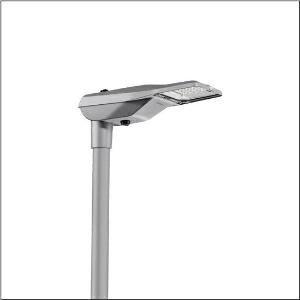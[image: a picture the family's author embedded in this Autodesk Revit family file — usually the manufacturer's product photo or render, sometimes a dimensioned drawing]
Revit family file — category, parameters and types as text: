
# Revit family: streetlight_sl_21_iq_micro___st1_0a_5xe1d31y08db_0307
name_source: partatom
category: Lighting Fixtures
units: mm (PartAtom-declared; Revit-internal decimal feet)

## family parameters
Cut with Voids When Loaded = No
Host = Face
Light Source = No
Part Type = Normal
Room Calculation Point = No
Round Connector Dimension = Use Diameter
Shared = No

## types (1)
- --- (1 x LED, 5110 lm, 39.1 W, 3000K)
    Apparent Load = 39 VA
    CIE Flux Codes = 37 72 97 100 100
    Color Rendering = 70
    Color Temperature = 3000K
    Default Elevation = 1800 mm
    Description = Streetlight SL 21 iQ micro, mast luminaire, primary light control with lens, of PMMA, primary optical cover: cover, of toughened safety glass, transparent, light distribution: ST1.0a, light emission: direct distribution, primary light characteristic: asymmetric, installation type: post-top, side-entry, LED, High Power LED, rated luminous flux: 5.110lm, luminous efficacy: 131lm/W, light colour: 730, colour temperature: 3000K, control: presetting dimming logarithmic, Street-Remote, Auto-Match, Temp-Guard, Lumen-Switch, Night-Set, Smart-Wire, Light-Fading, Desk-Remote (wireless, voltage-free reading and setting of iQ features in the workshop via application-optimized NFC function/RFID function), optimised constant luminous flux control (CLO 2.0), mains connection: 220..240V, AC, 50/60Hz, start of lifetime: 39W, end of service life: 41W, reduction: 17W, luminaire housing, of diecast aluminium, powder-coated, Siteco® metallic grey (DB 702S), corrosivity category C5 mid according to DIN EN ISO 12944, please order mast flange separately, inclination adjustable: 0°, 5°, 10°, 15°, sealing non-destructively replaceable, multi-level sealing system, length: 528mm, width: 235mm, height: 110mm, mast flange for spigot size: 42mm (side-entry): 5XC10008XM4, 60/48mm (side-entry/post-top): 5XC10108XM2, 76/60mm (side-entry/post-top): 5XC10108XM1, Smart Interface below and above, protection rating (complete): IP66, insulation class (complete): insulation class II (safety insulation), certification: CE, ENEC, ENEC+, VDE, impact resistance: IK09, permissible operating ambient temperature for outdoor applications: -40..+50°C, standard-compliant lighting for roads and squares, packaging unit: 1 piece

Light Distribution: ST1.0a
    Height = 110 mm
    Lamp = 1 x LED
    Lamp Light Flux = 5110 lm
    Lamp Power = 39.1 W
    Lamp count = 1
    Length = 528 mm
    Luminous efficacy = 131 lm/W
    Manufacturer = Siteco
    ModVariant = No
    Model = 5XE1D31Y08DB
    Number of Poles = 1
    OnlyDefault = Yes
    Power Factor = 1
    Product Name = Streetlight SL 21 iQ micro | ST1.0a
    Product group = mast luminaire | pylon top
    ProductGroupID = 6100
    Protection Class = Protection class II
    Protection Degree = IP 66
    RLX_Detail_Level = 1
    RLX_Emergency_Light_Flux = 0 lm
    RLX_Emergency_Type = 0
    RLX_Emergency_Type_DB = No
    RlxData = <blob elided: 98369 chars, md5=5723e704>
    Socket = socket
    Standby Power = 0 W
    System Light Flux = 5110 lm
    System Power = 39 W
    Type Comments = factory setting: luminous flux: 100 % | dim-lin: 254 | 765 mA
    Type Image = l_1007239.jpg
    URL = http://relux.com
    VarID = @adj_045457
    Voltage = 0 V
    Weight = 0.00 kg
    Width = 235 mm

## geometry (parser evidence)
native form markers: Blend x4, Sweep x11
no freeform markers — native parametric forms only
